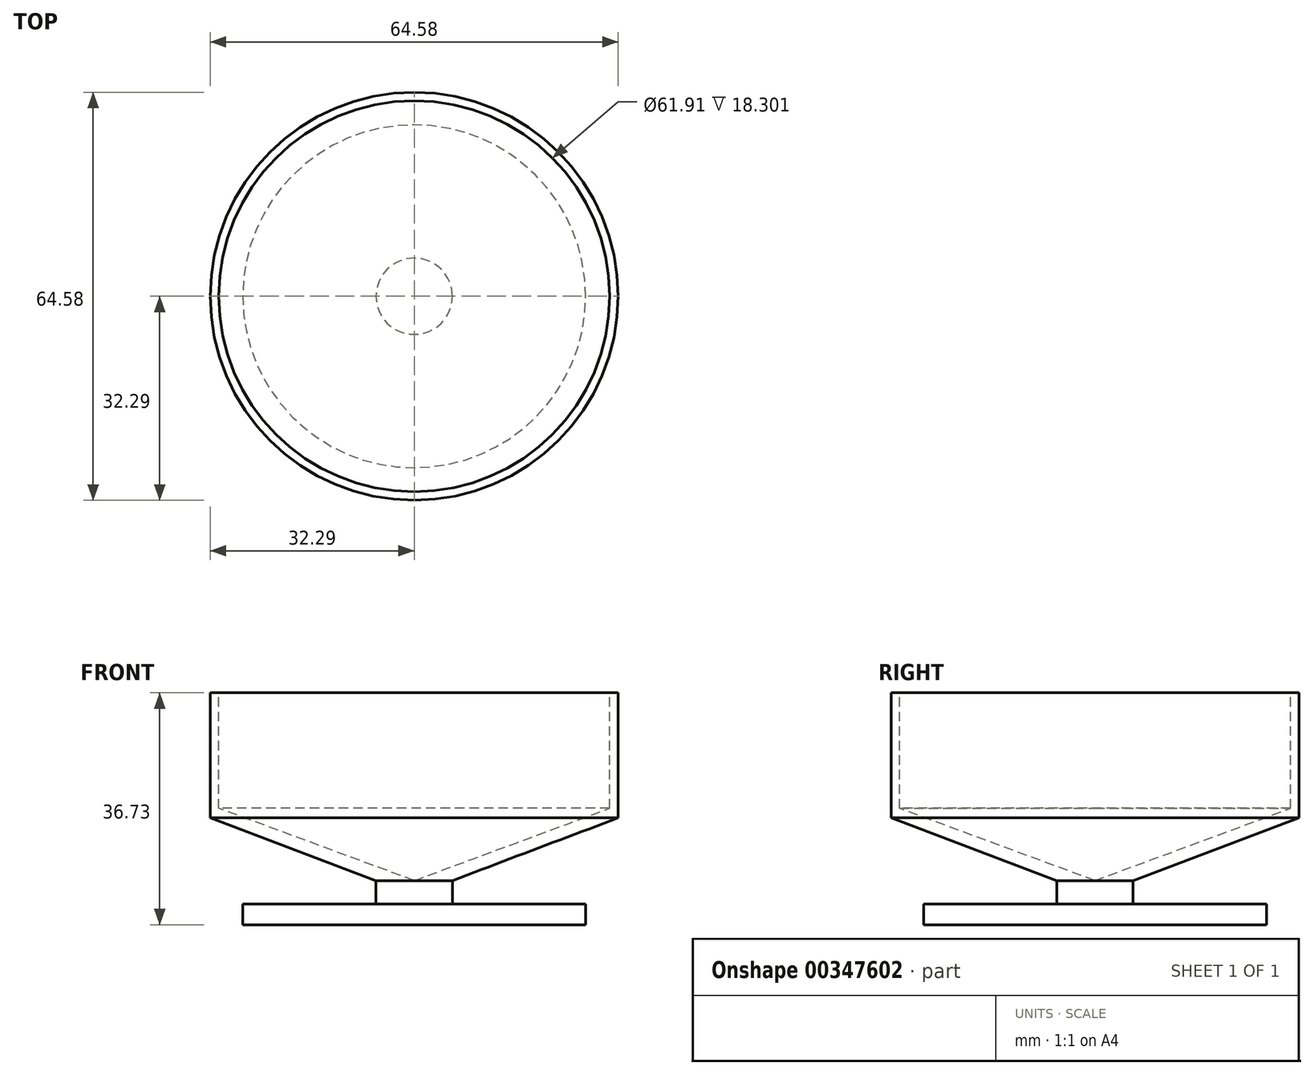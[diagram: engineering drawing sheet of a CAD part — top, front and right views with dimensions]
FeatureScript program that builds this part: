
annotation { "Feature Type Name" : "Feature", "Feature Type Description" : "" }
export const myFeature = defineFeature(function(context is Context, id is Id, definition is map)
    precondition{}
    {
        {
            var Q0;
            Q0=qCreatedBy(makeId("Front.planeOp"),FACE);
            var sketch = newSketch(context, id + "F0", { "sketchPlane" : qUnion([Q0])});
            skLineSegment(sketch, "E0", {"start": v(0, 0) * mm, "end": v(-27.14, 0) * mm});
            skLineSegment(sketch, "E1", {"start": v(-27.14, 0) * mm, "end": v(-27.14, 3.3) * mm});
            skLineSegment(sketch, "E2", {"start": v(-27.14, 3.3) * mm, "end": v(-6.04, 3.3) * mm});
            skLineSegment(sketch, "E3", {"start": v(-6.04, 3.3) * mm, "end": v(-6.04, 6.99) * mm});
            skLineSegment(sketch, "E4", {"start": v(0, 6.99) * mm, "end": v(0, 0) * mm});
            skLineSegment(sketch, "E5", {"start": v(-6.04, 6.99) * mm, "end": v(-32.3, 16.9) * mm});
            skLineSegment(sketch, "E6", {"start": v(-32.3, 16.9) * mm, "end": v(-32.3, 36.73) * mm});
            skLineSegment(sketch, "E7", {"start": v(-32.3, 36.73) * mm, "end": v(-30.95, 36.73) * mm});
            skLineSegment(sketch, "E8", {"start": v(-30.95, 36.73) * mm, "end": v(-30.95, 18.42) * mm});
            skLineSegment(sketch, "E9", {"start": v(-30.95, 18.42) * mm, "end": v(0, 6.99) * mm});
            skSolve(sketch);
        }
        {
            var Q0;
            Q0=makeQuery(id+"F0.imprint","IMPRINT",FACE,{"disambiguationData":[TD([[makeQuery(id+"F0.imprint","IMPRINT",EDGE,{"derivedFrom":sQuery(id+"F0.wireOp",EDGE,"E0")}),-1.0]])]});
            var Q1;
            Q1=sQuery(id+"F0.wireOp",EDGE,"E4");
            revolve(context, id + "F1", {"entities" : qUnion([Q0]), "axis" : qUnion([Q1]), "revolveType" : RevolveType.FULL});
        }
    });
